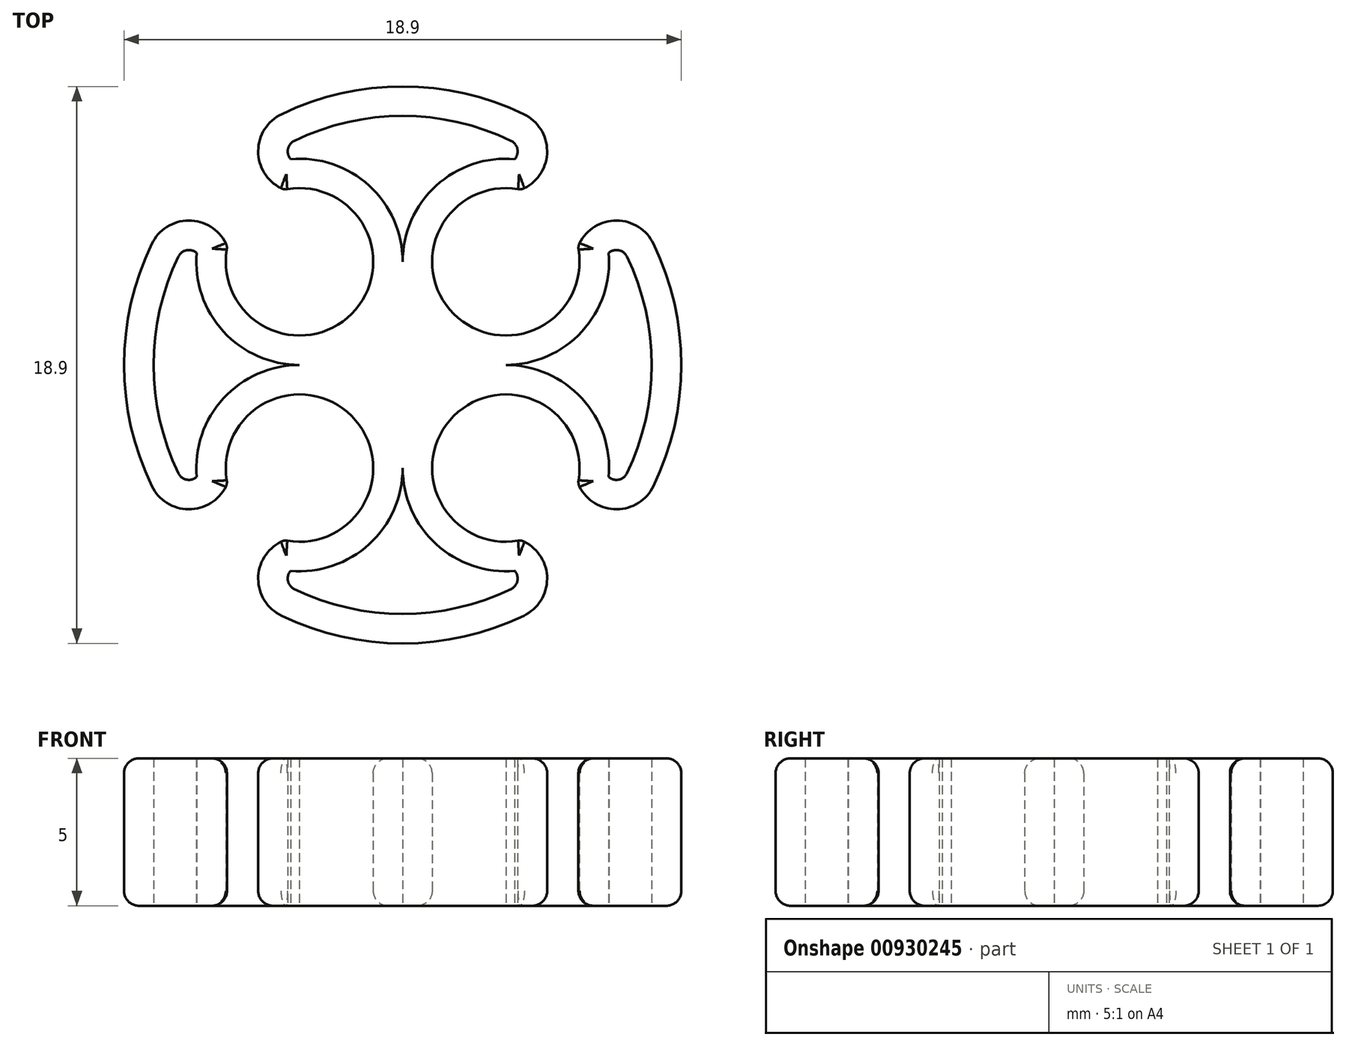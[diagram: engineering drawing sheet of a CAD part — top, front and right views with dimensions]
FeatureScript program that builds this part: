
annotation { "Feature Type Name" : "Feature", "Feature Type Description" : "" }
export const myFeature = defineFeature(function(context is Context, id is Id, definition is map)
    precondition{}
    {
        {
            var Q0;
            Q0=qCreatedBy(makeId("Top.planeOp"),FACE);
            var sketch = newSketch(context, id + "F0", { "sketchPlane" : qUnion([Q0])});
            skCircle(sketch, "E0", {"center": v(-7.6, 4.44) * mm, "radius": 2.5 * mm});
            skCircle(sketch, "E1.0.1.0", {"center": v(-7.6, 11.44) * mm, "radius": 2.5 * mm});
            skCircle(sketch, "E1.1.0.0", {"center": v(-0.6, 4.44) * mm, "radius": 2.5 * mm});
            skCircle(sketch, "E1.1.1.0", {"center": v(-0.6, 11.44) * mm, "radius": 2.5 * mm});
            skLineSegment(sketch, "E1.direction1", {"start": v(-7.6, 4.44) * mm, "end": v(-0.6, 4.44) * mm, "construction": true});
            skLineSegment(sketch, "E1.direction2", {"start": v(-7.6, 4.44) * mm, "end": v(-7.6, 11.44) * mm, "construction": true});
            skLineSegment(sketch, "E2.bottom", {"start": v(-7.6, 11.44) * mm, "end": v(-0.6, 11.44) * mm, "construction": true});
            skLineSegment(sketch, "E2.left", {"start": v(-7.6, 11.44) * mm, "end": v(-7.6, 4.44) * mm, "construction": true});
            skLineSegment(sketch, "E2.right", {"start": v(-0.6, 11.44) * mm, "end": v(-0.6, 4.44) * mm, "construction": true});
            skCircle(sketch, "E3", {"center": v(-4.1, 7.94) * mm, "radius": 9.45 * mm});
            skPoint(sketch, "E3.centerSnap0", {"position": v(-7.6, 7.94) * mm});
            skPoint(sketch, "E3.centerSnap1", {"position": v(-4.1, 11.44) * mm});
            skCircle(sketch, "E4", {"center": v(-7.6, 15.19) * mm, "radius": 1.4 * mm});
            skCircle(sketch, "E5", {"center": v(-11.35, 11.44) * mm, "radius": 1.4 * mm});
            skLineSegment(sketch, "E6", {"start": v(-4.1, 11.44) * mm, "end": v(-4.1, 4.44) * mm, "construction": true});
            skLineSegment(sketch, "E7", {"start": v(-4.1, 4.44) * mm, "end": v(-7.6, 7.94) * mm, "construction": true});
            skLineSegment(sketch, "E8", {"start": v(-0.6, 7.94) * mm, "end": v(-7.6, 7.94) * mm, "construction": true});
            skCircle(sketch, "E9.MirrorC", {"center": v(-0.6, 15.19) * mm, "radius": 1.4 * mm});
            skCircle(sketch, "E10.MirrorC", {"center": v(3.15, 11.44) * mm, "radius": 1.4 * mm});
            skCircle(sketch, "E11.MirrorC", {"center": v(-7.6, 0.7) * mm, "radius": 1.4 * mm});
            skCircle(sketch, "E12.MirrorC", {"center": v(-11.35, 4.44) * mm, "radius": 1.4 * mm});
            skCircle(sketch, "E13.MirrorC", {"center": v(-0.6, 0.7) * mm, "radius": 1.4 * mm});
            skCircle(sketch, "E14.MirrorC", {"center": v(3.15, 4.44) * mm, "radius": 1.4 * mm});
            skSolve(sketch);
        }
        {
            var Q0;
            {var subQ0=sQuery(id+"F0.wireOp",EDGE,"E3");var subQ10=sQuery(id+"F0.wireOp",EDGE,"E0");var subQ11=makeQuery(id+"F0.imprint","INTERSECT",VERTEX,{"disambiguationData":[OD(0.0)],"derivedFrom":[subQ10,subQ0]});Q0=makeQuery(id+"F0.imprint","IMPRINT",FACE,{"disambiguationData":[TD([[makeQuery(id+"F0.imprint","IMPRINT",EDGE,{"disambiguationData":[TD([[subQ11,1.0]])],"derivedFrom":subQ10}),-1.0]])]});}
            var Q1;
            {var subQ0=sQuery(id+"F0.wireOp",EDGE,"E4");var subQ1=sQuery(id+"F0.wireOp",EDGE,"E1.0.1.0");var subQ2=makeQuery(id+"F0.imprint","INTERSECT",VERTEX,{"disambiguationData":[OD(0.0)],"derivedFrom":[subQ1,subQ0]});Q1=makeQuery(id+"F0.imprint","IMPRINT",FACE,{"disambiguationData":[TD([[makeQuery(id+"F0.imprint","IMPRINT",EDGE,{"disambiguationData":[TD([[subQ2,1.0]])],"derivedFrom":subQ1}),-1.0]])]});}
            var Q2;
            {var subQ0=sQuery(id+"F0.wireOp",EDGE,"E5");var subQ1=sQuery(id+"F0.wireOp",EDGE,"E1.0.1.0");var subQ2=makeQuery(id+"F0.imprint","INTERSECT",VERTEX,{"disambiguationData":[OD(0.0)],"derivedFrom":[subQ1,subQ0]});Q2=makeQuery(id+"F0.imprint","IMPRINT",FACE,{"disambiguationData":[TD([[makeQuery(id+"F0.imprint","IMPRINT",EDGE,{"disambiguationData":[TD([[subQ2,-1.0]])],"derivedFrom":subQ1}),-1.0]])]});}
            var Q3;
            {var subQ0=sQuery(id+"F0.wireOp",EDGE,"E12.MirrorC");var subQ1=sQuery(id+"F0.wireOp",EDGE,"E0");var subQ2=makeQuery(id+"F0.imprint","INTERSECT",VERTEX,{"disambiguationData":[OD(0.0)],"derivedFrom":[subQ1,subQ0]});Q3=makeQuery(id+"F0.imprint","IMPRINT",FACE,{"disambiguationData":[TD([[makeQuery(id+"F0.imprint","IMPRINT",EDGE,{"disambiguationData":[TD([[subQ2,1.0]])],"derivedFrom":subQ1}),-1.0]])]});}
            var Q4;
            {var subQ0=sQuery(id+"F0.wireOp",EDGE,"E11.MirrorC");var subQ1=sQuery(id+"F0.wireOp",EDGE,"E0");var subQ2=makeQuery(id+"F0.imprint","INTERSECT",VERTEX,{"disambiguationData":[OD(0.0)],"derivedFrom":[subQ1,subQ0]});Q4=makeQuery(id+"F0.imprint","IMPRINT",FACE,{"disambiguationData":[TD([[makeQuery(id+"F0.imprint","IMPRINT",EDGE,{"disambiguationData":[TD([[subQ2,-1.0]])],"derivedFrom":subQ1}),-1.0]])]});}
            var Q5;
            {var subQ0=sQuery(id+"F0.wireOp",EDGE,"E9.MirrorC");var subQ1=sQuery(id+"F0.wireOp",EDGE,"E1.1.1.0");var subQ2=makeQuery(id+"F0.imprint","INTERSECT",VERTEX,{"disambiguationData":[OD(0.0)],"derivedFrom":[subQ1,subQ0]});Q5=makeQuery(id+"F0.imprint","IMPRINT",FACE,{"disambiguationData":[TD([[makeQuery(id+"F0.imprint","IMPRINT",EDGE,{"disambiguationData":[TD([[subQ2,-1.0]])],"derivedFrom":subQ1}),-1.0]])]});}
            var Q6;
            {var subQ0=sQuery(id+"F0.wireOp",EDGE,"E10.MirrorC");var subQ1=sQuery(id+"F0.wireOp",EDGE,"E1.1.1.0");var subQ2=makeQuery(id+"F0.imprint","INTERSECT",VERTEX,{"disambiguationData":[OD(0.0)],"derivedFrom":[subQ1,subQ0]});Q6=makeQuery(id+"F0.imprint","IMPRINT",FACE,{"disambiguationData":[TD([[makeQuery(id+"F0.imprint","IMPRINT",EDGE,{"disambiguationData":[TD([[subQ2,1.0]])],"derivedFrom":subQ1}),-1.0]])]});}
            var Q7;
            {var subQ0=sQuery(id+"F0.wireOp",EDGE,"E14.MirrorC");var subQ1=sQuery(id+"F0.wireOp",EDGE,"E1.1.0.0");var subQ2=makeQuery(id+"F0.imprint","INTERSECT",VERTEX,{"disambiguationData":[OD(0.0)],"derivedFrom":[subQ1,subQ0]});Q7=makeQuery(id+"F0.imprint","IMPRINT",FACE,{"disambiguationData":[TD([[makeQuery(id+"F0.imprint","IMPRINT",EDGE,{"disambiguationData":[TD([[subQ2,1.0]])],"derivedFrom":subQ1}),-1.0]])]});}
            var Q8;
            {var subQ0=sQuery(id+"F0.wireOp",EDGE,"E13.MirrorC");var subQ1=sQuery(id+"F0.wireOp",EDGE,"E1.1.0.0");var subQ2=makeQuery(id+"F0.imprint","INTERSECT",VERTEX,{"disambiguationData":[OD(0.0)],"derivedFrom":[subQ1,subQ0]});Q8=makeQuery(id+"F0.imprint","IMPRINT",FACE,{"disambiguationData":[TD([[makeQuery(id+"F0.imprint","IMPRINT",EDGE,{"disambiguationData":[TD([[subQ2,-1.0]])],"derivedFrom":subQ1}),-1.0]])]});}
            var Q9;
            {var subQ5=sQuery(id+"F0.wireOp",EDGE,"E12.MirrorC");var subQ6=sQuery(id+"F0.wireOp",EDGE,"E0");var subQ7=makeQuery(id+"F0.imprint","INTERSECT",VERTEX,{"disambiguationData":[OD(1.0)],"derivedFrom":[subQ6,subQ5]});Q9=makeQuery(id+"F0.imprint","IMPRINT",FACE,{"disambiguationData":[TD([[makeQuery(id+"F0.imprint","IMPRINT",EDGE,{"disambiguationData":[TD([[subQ7,1.0]])],"derivedFrom":subQ6}),-1.0]])]});}
            extrude(context, id + "F1", {"entities" : qUnion([Q0, Q1, Q2, Q3, Q4, Q5, Q6, Q7, Q8, Q9]), "depth" : 5 * mm, "offsetDistance" : 25 * mm});
        }
        {
            var Q0;
            {var subQ0=sQuery(id+"F0.wireOp",EDGE,"E3");var subQ1=sQuery(id+"F0.wireOp",EDGE,"E1.0.1.0");Q0=makeQuery(id+"F1.opExtrude","SWEPT_EDGE",EDGE,{"disambiguationData":[OSD([subQ1,subQ0]),TDD([makeQuery(id+"F0.imprint","INTERSECT",VERTEX,{"disambiguationData":[OD(0.0)],"derivedFrom":[subQ1,subQ0]})])]});}
            var Q1;
            {var subQ0=sQuery(id+"F0.wireOp",EDGE,"E3");var subQ1=sQuery(id+"F0.wireOp",EDGE,"E1.0.1.0");Q1=makeQuery(id+"F1.opExtrude","SWEPT_EDGE",EDGE,{"disambiguationData":[OSD([subQ1,subQ0]),TDD([makeQuery(id+"F0.imprint","INTERSECT",VERTEX,{"disambiguationData":[OD(1.0)],"derivedFrom":[subQ1,subQ0]})])]});}
            var Q2;
            {var subQ0=sQuery(id+"F0.wireOp",EDGE,"E3");var subQ1=sQuery(id+"F0.wireOp",EDGE,"E0");Q2=makeQuery(id+"F1.opExtrude","SWEPT_EDGE",EDGE,{"disambiguationData":[OSD([subQ1,subQ0]),TDD([makeQuery(id+"F0.imprint","INTERSECT",VERTEX,{"disambiguationData":[OD(0.0)],"derivedFrom":[subQ1,subQ0]})])]});}
            var Q3;
            {var subQ0=sQuery(id+"F0.wireOp",EDGE,"E3");var subQ1=sQuery(id+"F0.wireOp",EDGE,"E0");Q3=makeQuery(id+"F1.opExtrude","SWEPT_EDGE",EDGE,{"disambiguationData":[OSD([subQ1,subQ0]),TDD([makeQuery(id+"F0.imprint","INTERSECT",VERTEX,{"disambiguationData":[OD(1.0)],"derivedFrom":[subQ1,subQ0]})])]});}
            var Q4;
            {var subQ0=sQuery(id+"F0.wireOp",EDGE,"E3");var subQ1=sQuery(id+"F0.wireOp",EDGE,"E1.1.0.0");Q4=makeQuery(id+"F1.opExtrude","SWEPT_EDGE",EDGE,{"disambiguationData":[OSD([subQ1,subQ0]),TDD([makeQuery(id+"F0.imprint","INTERSECT",VERTEX,{"disambiguationData":[OD(0.0)],"derivedFrom":[subQ1,subQ0]})])]});}
            var Q5;
            {var subQ0=sQuery(id+"F0.wireOp",EDGE,"E3");var subQ1=sQuery(id+"F0.wireOp",EDGE,"E1.1.0.0");Q5=makeQuery(id+"F1.opExtrude","SWEPT_EDGE",EDGE,{"disambiguationData":[OSD([subQ1,subQ0]),TDD([makeQuery(id+"F0.imprint","INTERSECT",VERTEX,{"disambiguationData":[OD(1.0)],"derivedFrom":[subQ1,subQ0]})])]});}
            var Q6;
            {var subQ0=sQuery(id+"F0.wireOp",EDGE,"E3");var subQ1=sQuery(id+"F0.wireOp",EDGE,"E1.1.1.0");Q6=makeQuery(id+"F1.opExtrude","SWEPT_EDGE",EDGE,{"disambiguationData":[OSD([subQ1,subQ0]),TDD([makeQuery(id+"F0.imprint","INTERSECT",VERTEX,{"disambiguationData":[OD(1.0)],"derivedFrom":[subQ1,subQ0]})])]});}
            var Q7;
            {var subQ0=sQuery(id+"F0.wireOp",EDGE,"E3");var subQ1=sQuery(id+"F0.wireOp",EDGE,"E1.1.1.0");Q7=makeQuery(id+"F1.opExtrude","SWEPT_EDGE",EDGE,{"disambiguationData":[OSD([subQ1,subQ0]),TDD([makeQuery(id+"F0.imprint","INTERSECT",VERTEX,{"disambiguationData":[OD(0.0)],"derivedFrom":[subQ1,subQ0]})])]});}
            fillet(context, id + "F2", {"entities" : qUnion([Q0, Q1, Q2, Q3, Q4, Q5, Q6, Q7]), "radius" : 0.35 * mm, "tangentPropagation" : true, "allowEdgeOverflow" : false});
        }
        {
            var Q0;
            Q0=makeQuery(id+"F1.opExtrude","CAP_FACE",FACE,{"disambiguationData":[OSD([sQuery(id+"F0.wireOp",EDGE,"E0"),sQuery(id+"F0.wireOp",EDGE,"E1.0.1.0"),sQuery(id+"F0.wireOp",EDGE,"E1.1.0.0"),sQuery(id+"F0.wireOp",EDGE,"E1.1.1.0"),sQuery(id+"F0.wireOp",EDGE,"E3")])],"isStart":false});
            var Q1;
            Q1=makeQuery(id+"F1.opExtrude","CAP_FACE",FACE,{"disambiguationData":[OSD([sQuery(id+"F0.wireOp",EDGE,"E0"),sQuery(id+"F0.wireOp",EDGE,"E1.0.1.0"),sQuery(id+"F0.wireOp",EDGE,"E1.1.0.0"),sQuery(id+"F0.wireOp",EDGE,"E1.1.1.0"),sQuery(id+"F0.wireOp",EDGE,"E3")])],"isStart":true});
            fillet(context, id + "F3", {"entities" : qUnion([Q0, Q1]), "radius" : 0.5 * mm, "tangentPropagation" : true, "allowEdgeOverflow" : false});
        }
        {
            var Q0;
            Q0=makeQuery(id+"F1.opExtrude","CAP_FACE",FACE,{"disambiguationData":[OSD([sQuery(id+"F0.wireOp",EDGE,"E0"),sQuery(id+"F0.wireOp",EDGE,"E1.0.1.0"),sQuery(id+"F0.wireOp",EDGE,"E1.1.0.0"),sQuery(id+"F0.wireOp",EDGE,"E1.1.1.0"),sQuery(id+"F0.wireOp",EDGE,"E3"),sQuery(id+"F0.wireOp",EDGE,"E4"),sQuery(id+"F0.wireOp",EDGE,"E5"),sQuery(id+"F0.wireOp",EDGE,"E9.MirrorC"),sQuery(id+"F0.wireOp",EDGE,"E10.MirrorC"),sQuery(id+"F0.wireOp",EDGE,"E11.MirrorC"),sQuery(id+"F0.wireOp",EDGE,"E12.MirrorC"),sQuery(id+"F0.wireOp",EDGE,"E13.MirrorC"),sQuery(id+"F0.wireOp",EDGE,"E14.MirrorC")])],"isStart":false});
            var Q1;
            Q1=makeQuery(id+"F1.opExtrude","CAP_FACE",FACE,{"disambiguationData":[OSD([sQuery(id+"F0.wireOp",EDGE,"E0"),sQuery(id+"F0.wireOp",EDGE,"E1.0.1.0"),sQuery(id+"F0.wireOp",EDGE,"E1.1.0.0"),sQuery(id+"F0.wireOp",EDGE,"E1.1.1.0"),sQuery(id+"F0.wireOp",EDGE,"E3"),sQuery(id+"F0.wireOp",EDGE,"E4"),sQuery(id+"F0.wireOp",EDGE,"E5"),sQuery(id+"F0.wireOp",EDGE,"E9.MirrorC"),sQuery(id+"F0.wireOp",EDGE,"E10.MirrorC"),sQuery(id+"F0.wireOp",EDGE,"E11.MirrorC"),sQuery(id+"F0.wireOp",EDGE,"E12.MirrorC"),sQuery(id+"F0.wireOp",EDGE,"E13.MirrorC"),sQuery(id+"F0.wireOp",EDGE,"E14.MirrorC")])],"isStart":true});
            shell(context, id + "F4", {"entities" : qUnion([Q0, Q1]), "thickness" : 1 * mm});
        }
    });
